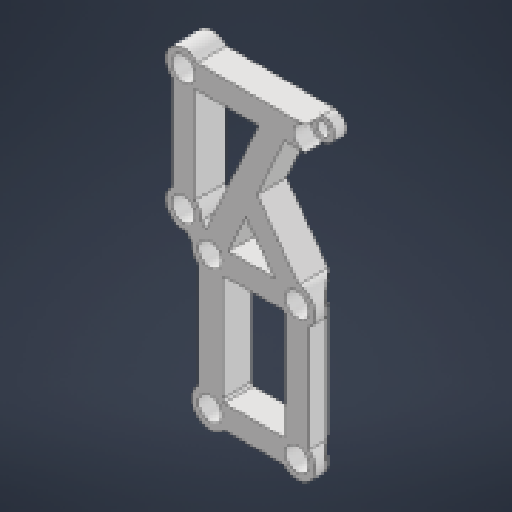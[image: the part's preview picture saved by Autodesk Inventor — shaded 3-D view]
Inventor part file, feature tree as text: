
AUTODESK INVENTOR PART (.ipt)
format: ipt  version: 2025 (Build 290162000, 162)  size: 301,056 bytes
history: native  units: mm
features: reference x11, other x10, extrude x5, sketch x5, plane x1
ambient origin geometry x8: Origin, YZ Plane, XZ Plane, XY Plane, X Axis, Y Axis, Z Axis, Center Point
bodies: Solid1 (feature_tree)
feature tree (32):
  extrude  "Extrusion1"  Depth=3.0mm
  plane  "Work Plane1"
  extrude  "Extrusion2"  Depth=3.0mm
  extrude  "Extrusion6"  Depth=6.0mm
  extrude  "Extrusion7"  Depth=6.0mm
  extrude  "Extrusion8"  Depth=6.0mm
  sketch  "Sketch1"  dims[d0=3.0mm d1=3.0mm]
  reference  "Reference1"
  reference  "Reference2"
  reference  "Reference3"
  reference  "Reference4"
  reference  "Reference5"
  reference  "Reference6"
  reference  "Reference7"
  reference  "Reference8"
  sketch  "Sketch2"  dims[d2=3.0mm d3=3.0mm]
  sketch  "Sketch6"  dims[d6=3.0mm d7=6.0mm]
  sketch  "Sketch7"  dims[d8=6.0mm d9=6.0mm]
  reference  "Reference9"
  reference  "Reference10"
  reference  "Reference11"
  sketch  "Sketch8"  dims[d10=6.0mm d14=6.0mm d15=6.0mm d16=8.0mm d17=0.0mm d19=11.0mm d20=22.75mm d21=0.0mm d35=6.0mm d36=6.0mm d37=6.0mm d38=3.5mm d39=0.0mm d41=6.0mm d42=9.5mm d43=0.0mm d44=3.2mm d45=3.2mm d46=3.0mm d47=3.0mm d48=6.0mm d49=6.0mm d50=6.0mm d51=6.0mm d52=6.0mm d53=6.0mm d54=6.0mm d55=3.0mm d56=0.0mm d57=6.0mm]
  other  "<userpath> 7 was better\Documents\ReplicatorPlusConversion\CAD\hotend.iam"
  other  "hotend.iam"
  other  "makerbot-shroud:1"
  other  "E3D_Hemera_Final_SWFix:1"
  other  "Nema 17 Stepper:1"
  other  "M3 Square Nut:4"
  other  "M3 Square Nut:3"
  other  "M3 Square Nut:6"
  other  "M3 Square Nut:7"
  other  "Hemera_XS_Reference_CAD:1"
